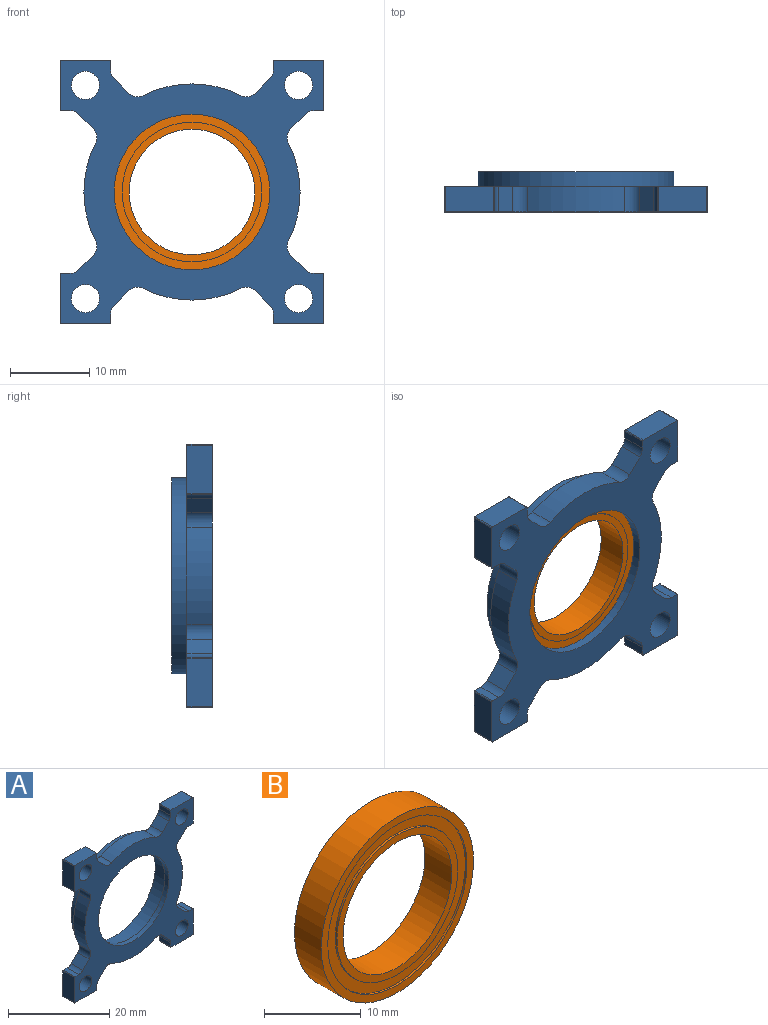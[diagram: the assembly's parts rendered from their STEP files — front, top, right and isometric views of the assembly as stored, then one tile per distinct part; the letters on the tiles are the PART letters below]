
ASSEMBLY  parts=2 mates=1
PART A: 67 faces, bbox 33.3x5.1x33.3 mm
  f0: cylinder r=9.84mm len=19.69mm, axis (0,1,0), area 69.1mm2, adj f38,f66
  f1: cylinder r=11.11mm len=22.23mm, axis (0,-1,0), area 276.7mm2, adj f65,f66
  f2: cylinder r=12.39mm len=24.78mm, axis (0,-1,0), area 148.3mm2, adj f10,f65
  f3: cylinder r=1.59mm len=3.18mm, axis (0,-1,0), area 6.3mm2, adj f10,f23,f24,f38
  f4: cylinder r=1.59mm len=3.18mm, axis (0,-1,0), area 6.3mm2, adj f10,f22,f23,f38
  f5: cylinder r=1.78mm len=3.56mm, axis (0,1,0), area 35.5mm2, adj f10,f38
  f6: cylinder r=1.78mm len=3.56mm, axis (0,1,0), area 35.5mm2, adj f10,f38
  f7: cylinder r=1.78mm len=3.56mm, axis (0,1,0), area 35.5mm2, adj f10,f38
  f8: cylinder r=1.78mm len=3.56mm, axis (0,1,0), area 35.5mm2, adj f10,f38
  f9: cylinder r=13.66mm len=12.32mm, axis (0,-1,0), area 40.6mm2, adj f10,f38,f61,f62
  f10: plane 33.27x33.27mm, normal (0,1,0), area 294.1mm2, adj f2,f3,f4,f5,f6,f7,f8,f9
  f11: plane 3.18x1.08mm, normal (1,0,0), area 3.4mm2, adj f10,f38,f48,f54
  f12: plane 6.1x3.18mm, normal (0,0,-1), area 19.4mm2, adj f10,f38,f48,f49
  f13: plane 6.1x3.18mm, normal (-1,0,0), area 19.4mm2, adj f10,f38,f49,f50
  f14: plane 3.18x1.08mm, normal (0,0,1), area 3.4mm2, adj f10,f38,f50,f53
  f15: plane 3.18x1.82mm, normal (-0.71,0,0.71), area 8.2mm2, adj f10,f38,f53,f63
  f16: cylinder r=13.66mm len=12.32mm, axis (0,-1,0), area 40.6mm2, adj f10,f38,f63,f64
  f17: plane 3.18x1.82mm, normal (-0.71,0,-0.71), area 8.2mm2, adj f10,f38,f52,f64
  f18: plane 3.18x1.08mm, normal (0,0,-1), area 3.4mm2, adj f10,f38,f39,f52
  f19: plane 6.1x3.18mm, normal (-1,0,0), area 19.4mm2, adj f10,f38,f39,f40
  f20: plane 6.1x3.18mm, normal (0,0,1), area 19.4mm2, adj f10,f38,f40,f43
  f21: plane 3.18x1.08mm, normal (1,0,0), area 3.4mm2, adj f10,f38,f43,f51
  f22: plane 3.18x1.82mm, normal (0.71,0,0.71), area 8.2mm2, adj f4,f10,f38,f51
  f23: cylinder r=13.66mm len=12.32mm, axis (0,-1,0), area 40.6mm2, adj f3,f4,f10,f38
  f24: plane 3.18x1.82mm, normal (-0.71,0,0.71), area 8.2mm2, adj f3,f10,f38,f58
  f25: plane 3.18x1.08mm, normal (-1,0,0), area 3.4mm2, adj f10,f38,f41,f58
  f26: plane 6.1x3.18mm, normal (0,0,1), area 19.4mm2, adj f10,f38,f41,f44
  f27: plane 6.1x3.18mm, normal (1,0,0), area 19.4mm2, adj f10,f38,f44,f45
  f28: plane 3.18x1.08mm, normal (0,0,-1), area 3.4mm2, adj f10,f38,f45,f57
  f29: plane 3.18x1.82mm, normal (0.71,0,-0.71), area 8.2mm2, adj f10,f38,f57,f59
  f30: cylinder r=13.66mm len=12.32mm, axis (0,-1,0), area 40.6mm2, adj f10,f38,f59,f60
  f31: plane 3.18x1.82mm, normal (0.71,0,0.71), area 8.2mm2, adj f10,f38,f56,f60
  f32: plane 3.18x1.08mm, normal (0,0,1), area 3.4mm2, adj f10,f38,f46,f56
  f33: plane 6.1x3.18mm, normal (1,0,0), area 19.4mm2, adj f10,f38,f46,f47
  f34: plane 6.1x3.18mm, normal (0,0,-1), area 19.4mm2, adj f10,f38,f42,f47
  f35: plane 3.18x1.08mm, normal (-1,0,0), area 3.4mm2, adj f10,f38,f42,f55
  f36: plane 3.18x1.82mm, normal (-0.71,0,-0.71), area 8.2mm2, adj f10,f38,f55,f62
  f37: plane 3.18x1.82mm, normal (0.71,0,-0.71), area 8.2mm2, adj f10,f38,f54,f61
  f38: plane 33.27x33.27mm, normal (0,-1,0), area 472.2mm2, adj f0,f3,f4,f5,f6,f7,f8,f9
  f39: cylinder r=0.13mm len=3.18mm, axis (0,-1,0), area 0.6mm2, adj f10,f18,f19,f38
  f40: cylinder r=0.13mm len=3.18mm, axis (0,1,0), area 0.6mm2, adj f10,f19,f20,f38
  f41: cylinder r=0.13mm len=3.18mm, axis (0,1,0), area 0.6mm2, adj f10,f25,f26,f38
  f42: cylinder r=0.13mm len=3.18mm, axis (0,1,0), area 0.6mm2, adj f10,f34,f35,f38
  f43: cylinder r=0.13mm len=3.18mm, axis (0,-1,0), area 0.6mm2, adj f10,f20,f21,f38
  f44: cylinder r=0.13mm len=3.18mm, axis (0,-1,0), area 0.6mm2, adj f10,f26,f27,f38
  f45: cylinder r=0.13mm len=3.18mm, axis (0,-1,0), area 0.6mm2, adj f10,f27,f28,f38
  f46: cylinder r=0.13mm len=3.18mm, axis (0,-1,0), area 0.6mm2, adj f10,f32,f33,f38
  f47: cylinder r=0.13mm len=3.18mm, axis (0,-1,0), area 0.6mm2, adj f10,f33,f34,f38
  f48: cylinder r=0.13mm len=3.18mm, axis (0,-1,0), area 0.6mm2, adj f10,f11,f12,f38
  f49: cylinder r=0.13mm len=3.18mm, axis (0,-1,0), area 0.6mm2, adj f10,f12,f13,f38
  f50: cylinder r=0.13mm len=3.18mm, axis (0,1,0), area 0.6mm2, adj f10,f13,f14,f38
  f51: cylinder r=1.59mm len=3.18mm, axis (0,-1,0), area 4mm2, adj f10,f21,f22,f38
  f52: cylinder r=1.59mm len=3.18mm, axis (0,-1,0), area 4mm2, adj f10,f17,f18,f38
  f53: cylinder r=1.59mm len=3.18mm, axis (0,-1,0), area 4mm2, adj f10,f14,f15,f38
  f54: cylinder r=1.59mm len=3.18mm, axis (0,-1,0), area 4mm2, adj f10,f11,f37,f38
  f55: cylinder r=1.59mm len=3.18mm, axis (0,-1,0), area 4mm2, adj f10,f35,f36,f38
  f56: cylinder r=1.59mm len=3.18mm, axis (0,-1,0), area 4mm2, adj f10,f31,f32,f38
  f57: cylinder r=1.59mm len=3.18mm, axis (0,-1,0), area 4mm2, adj f10,f28,f29,f38
  f58: cylinder r=1.59mm len=3.18mm, axis (0,-1,0), area 4mm2, adj f10,f24,f25,f38
  f59: cylinder r=1.59mm len=3.18mm, axis (0,-1,0), area 6.3mm2, adj f10,f29,f30,f38
  f60: cylinder r=1.59mm len=3.18mm, axis (0,-1,0), area 6.3mm2, adj f10,f30,f31,f38
  f61: cylinder r=1.59mm len=3.18mm, axis (0,-1,0), area 6.3mm2, adj f9,f10,f37,f38
  f62: cylinder r=1.59mm len=3.18mm, axis (0,-1,0), area 6.3mm2, adj f9,f10,f36,f38
  f63: cylinder r=1.59mm len=3.18mm, axis (0,-1,0), area 6.3mm2, adj f10,f15,f16,f38
  f64: cylinder r=1.59mm len=3.18mm, axis (0,-1,0), area 6.3mm2, adj f10,f16,f17,f38
  f65: plane 24.78x24.78mm, normal (0,1,0), area 94.4mm2, adj f1,f2
  f66: plane 22.23x22.23mm, normal (0,1,0), area 83.6mm2, adj f0,f1
PART B: 12 faces, bbox 22.2x3.9x22.2 mm
  f0: cylinder r=8.83mm len=17.65mm, axis (0,-1,0), area 14.1mm2, adj f6,f11
  f1: cylinder r=10.16mm len=20.32mm, axis (0,-1,0), area 16.2mm2, adj f9,f11
  f2: cylinder r=8.83mm len=17.65mm, axis (0,1,0), area 14.1mm2, adj f7,f10
  f3: cylinder r=10.16mm len=20.32mm, axis (0,1,0), area 16.2mm2, adj f8,f10
  f4: cylinder r=7.94mm len=15.88mm, axis (0,-1,0), area 195.1mm2, adj f6,f7
  f5: cylinder r=11.11mm len=22.23mm, axis (0,-1,0), area 273.1mm2, adj f8,f9
  f6: plane 17.65x17.65mm, normal (0,-1,0), area 46.8mm2, adj f0,f4
  f7: plane 17.65x17.65mm, normal (0,1,0), area 46.8mm2, adj f2,f4
  f8: plane 22.23x22.23mm, normal (0,1,0), area 63.7mm2, adj f3,f5
  f9: plane 22.23x22.23mm, normal (0,-1,0), area 63.7mm2, adj f1,f5
  f10: plane 20.32x20.32mm, normal (0,1,0), area 79.5mm2, adj f2,f3
  f11: plane 20.32x20.32mm, normal (0,-1,0), area 79.5mm2, adj f0,f1
PLACE A t=(9.41,15.04,26.98)mm
PLACE B rot(axis=(0,1,0),0deg) t=(9.41,16.16,26.98)mm
MATE fastened B.f0 <-> A.f0  axis (0,-1,0) through (9.41,16.42,26.98)mm
